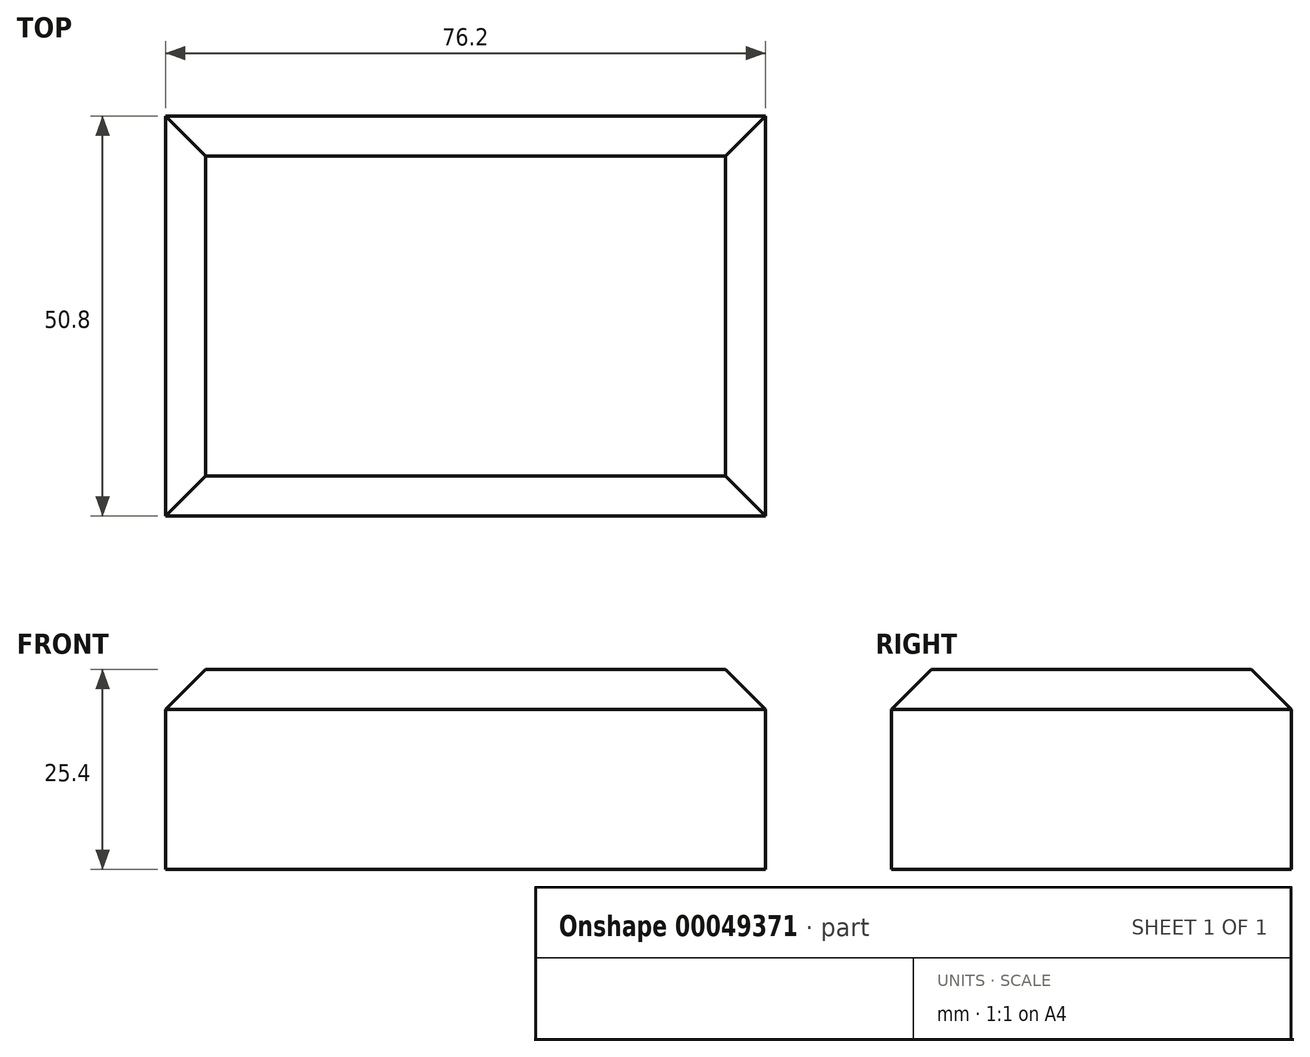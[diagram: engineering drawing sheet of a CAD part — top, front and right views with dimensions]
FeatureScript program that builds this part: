
annotation { "Feature Type Name" : "Feature", "Feature Type Description" : "" }
export const myFeature = defineFeature(function(context is Context, id is Id, definition is map)
    precondition{}
    {
        {
            var Q0;
            Q0=qCreatedBy(makeId("Top.planeOp"),FACE);
            var sketch = newSketch(context, id + "F0", { "sketchPlane" : qUnion([Q0])});
            skLineSegment(sketch, "E0.bottom", {"start": v(0, 0) * mm, "end": v(76.2, 0) * mm});
            skLineSegment(sketch, "E0.top", {"start": v(0, -50.8) * mm, "end": v(76.2, -50.8) * mm});
            skLineSegment(sketch, "E0.left", {"start": v(0, 0) * mm, "end": v(0, -50.8) * mm});
            skLineSegment(sketch, "E0.right", {"start": v(76.2, 0) * mm, "end": v(76.2, -50.8) * mm});
            skSolve(sketch);
        }
        {
            var Q0;
            Q0 = qSketchRegion(id + "F0", true);
            extrude(context, id + "F1", {"entities" : qUnion([Q0]), "depth" : 25.4 * mm});
        }
        {
            var Q0;
            Q0=makeQuery(id+"F1.opExtrude","CAP_FACE",FACE,{"disambiguationData":[OSD([sQuery(id+"F0.wireOp",EDGE,"E0.bottom"),sQuery(id+"F0.wireOp",EDGE,"E0.top"),sQuery(id+"F0.wireOp",EDGE,"E0.left"),sQuery(id+"F0.wireOp",EDGE,"E0.right")])],"isStart":false});
            chamfer(context, id + "F2", {"entities" : qUnion([Q0]), "width" : 5.08 * mm, "tangentPropagation" : true});
        }
    });
